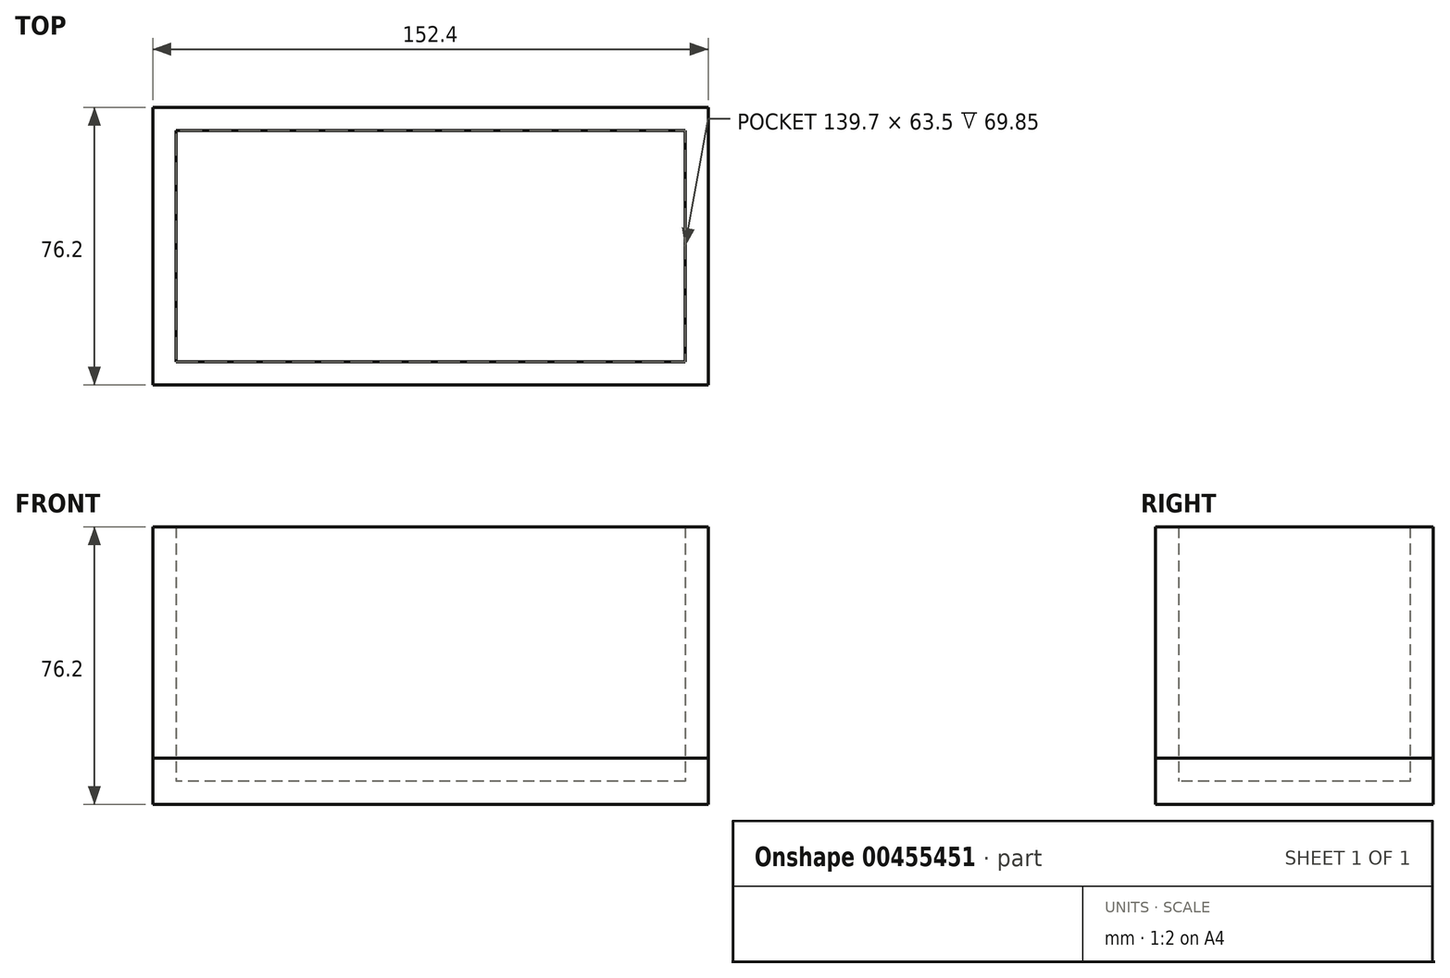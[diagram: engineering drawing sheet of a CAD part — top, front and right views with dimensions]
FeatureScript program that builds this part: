
annotation { "Feature Type Name" : "Feature", "Feature Type Description" : "" }
export const myFeature = defineFeature(function(context is Context, id is Id, definition is map)
    precondition{}
    {
        {
            var Q0;
            Q0=qCreatedBy(makeId("Top.planeOp"),FACE);
            var sketch = newSketch(context, id + "F0", { "sketchPlane" : qUnion([Q0])});
            skLineSegment(sketch, "E0.bottom", {"start": v(76.2, 38.1) * mm, "end": v(-76.2, 38.1) * mm});
            skLineSegment(sketch, "E0.top", {"start": v(76.2, -38.1) * mm, "end": v(-76.2, -38.1) * mm});
            skLineSegment(sketch, "E0.left", {"start": v(76.2, 38.1) * mm, "end": v(76.2, -38.1) * mm});
            skLineSegment(sketch, "E0.right", {"start": v(-76.2, 38.1) * mm, "end": v(-76.2, -38.1) * mm});
            skPoint(sketch, "E0.middle", {"position": v(0, 0) * mm});
            skSolve(sketch);
        }
        {
            var Q0;
            Q0 = qSketchRegion(id + "F0", true);
            extrude(context, id + "F1", {"entities" : qUnion([Q0]), "depth" : 76.2 * mm});
        }
        {
            var Q0;
            Q0=makeQuery(id+"F1.opExtrude","CAP_FACE",FACE,{"disambiguationData":[OSD([sQuery(id+"F0.wireOp",EDGE,"E0.bottom"),sQuery(id+"F0.wireOp",EDGE,"E0.top"),sQuery(id+"F0.wireOp",EDGE,"E0.left"),sQuery(id+"F0.wireOp",EDGE,"E0.right")])],"isStart":false});
            shell(context, id + "F2", {"entities" : qUnion([Q0]), "thickness" : 6.35 * mm});
        }
        {
            var Q0;
            Q0=qCreatedBy(makeId("Top.planeOp"),FACE);
            var sketch = newSketch(context, id + "F3", { "sketchPlane" : qUnion([Q0])});
            skLineSegment(sketch, "E1.bottom", {"start": v(76.2, 38.1) * mm, "end": v(-76.2, 38.1) * mm});
            skLineSegment(sketch, "E1.top", {"start": v(76.2, -38.1) * mm, "end": v(-76.2, -38.1) * mm});
            skLineSegment(sketch, "E1.left", {"start": v(76.2, 38.1) * mm, "end": v(76.2, -38.1) * mm});
            skLineSegment(sketch, "E1.right", {"start": v(-76.2, 38.1) * mm, "end": v(-76.2, -38.1) * mm});
            skPoint(sketch, "E1.middle", {"position": v(0, 0) * mm});
            skSolve(sketch);
        }
        {
            var Q0;
            Q0 = qSketchRegion(id + "F3", true);
            extrude(context, id + "F4", {"entities" : qUnion([Q0]), "depth" : 12.7 * mm});
        }
    });
